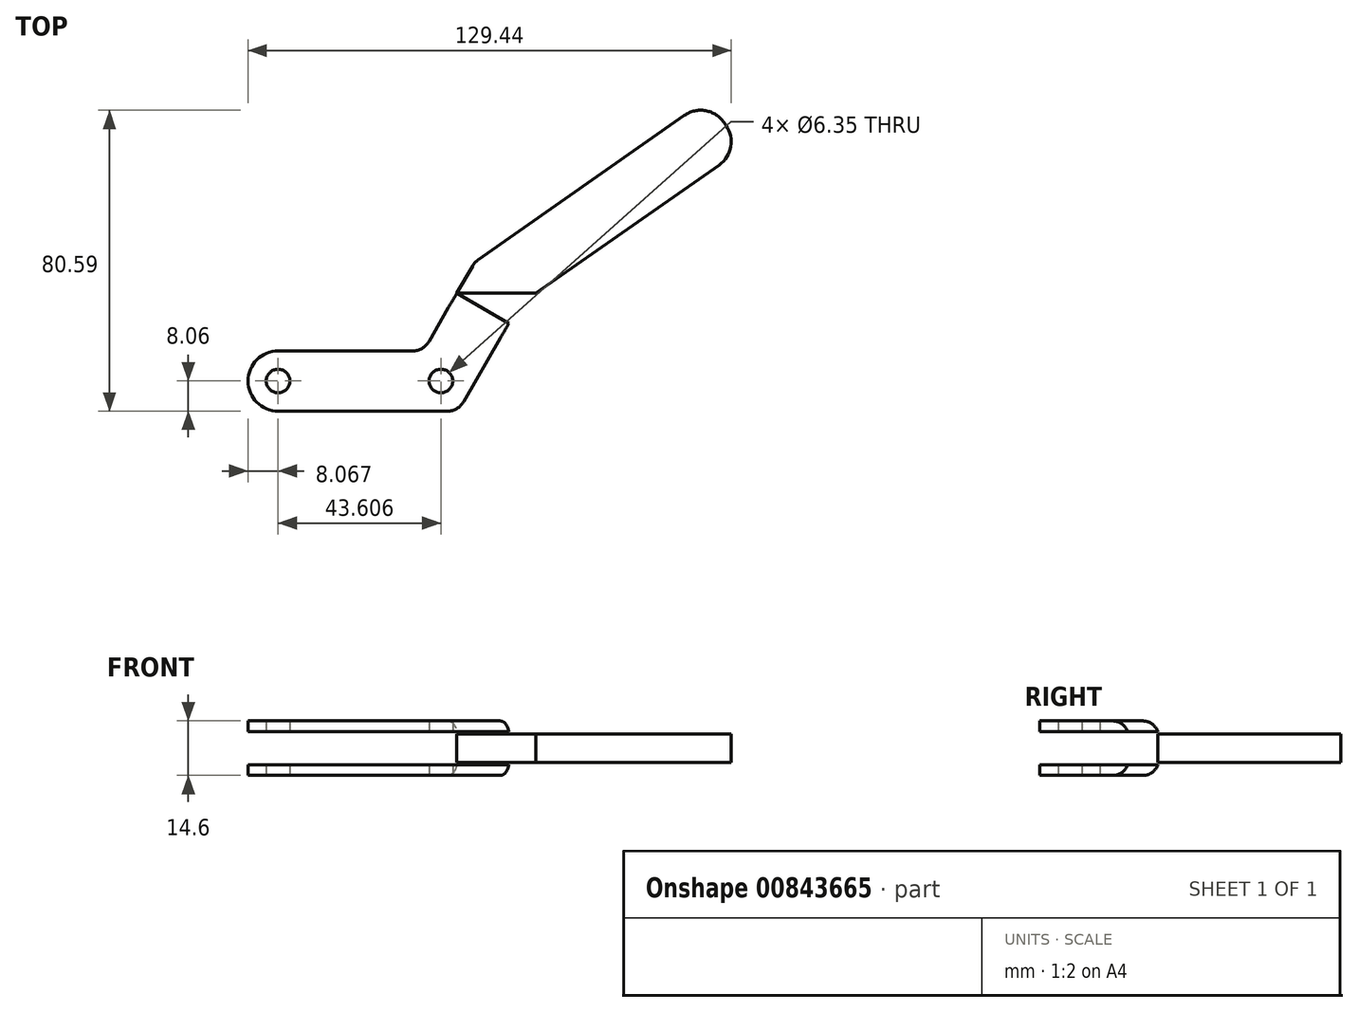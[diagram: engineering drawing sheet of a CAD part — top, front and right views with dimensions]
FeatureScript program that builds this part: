
annotation { "Feature Type Name" : "Feature", "Feature Type Description" : "" }
export const myFeature = defineFeature(function(context is Context, id is Id, definition is map)
    precondition{}
    {
        {
            var Q0;
            Q0=qCreatedBy(makeId("Top.planeOp"),FACE);
            var sketch = newSketch(context, id + "F0", { "sketchPlane" : qUnion([Q0])});
            skLineSegment(sketch, "E0.bottom", {"start": v(21.8, 8.06) * mm, "end": v(-21.8, 8.06) * mm});
            skLineSegment(sketch, "E0.top", {"start": v(21.8, -8.06) * mm, "end": v(-21.8, -8.06) * mm, "construction": true});
            skPoint(sketch, "E0.middle", {"position": v(0, 0) * mm});
            skArc(sketch, "E1", {"start": v(-21.8, 8.06) * mm, "mid": v(-29.87, 0) * mm, "end": v(-21.8, -8.06) * mm});
            skLineSegment(sketch, "E2", {"start": v(14.35, 3.22) * mm, "end": v(30.86, 31.82) * mm, "construction": true});
            skLineSegment(sketch, "E3", {"start": v(42.97, 20.53) * mm, "end": v(26.46, -8.06) * mm});
            skLineSegment(sketch, "E4", {"start": v(26.46, -8.06) * mm, "end": v(14.35, 3.22) * mm, "construction": true});
            skLineSegment(sketch, "E5", {"start": v(30.86, 31.82) * mm, "end": v(42.97, 20.53) * mm, "construction": true});
            skLineSegment(sketch, "E6", {"start": v(30.86, 31.82) * mm, "end": v(93.28, 75.53) * mm});
            skLineSegment(sketch, "E7", {"start": v(102.57, 62.26) * mm, "end": v(42.97, 20.53) * mm});
            skCircle(sketch, "E8", {"center": v(-21.8, 0) * mm, "radius": 3.18 * mm});
            skCircle(sketch, "E9", {"center": v(21.8, 0) * mm, "radius": 3.18 * mm});
            skLineSegment(sketch, "E10", {"start": v(26.46, -8.06) * mm, "end": v(21.8, -8.06) * mm});
            skLineSegment(sketch, "E11", {"start": v(21.8, -8.06) * mm, "end": v(-21.8, -8.06) * mm});
            skLineSegment(sketch, "E12", {"start": v(-21.8, 8.06) * mm, "end": v(17.15, 8.06) * mm});
            skLineSegment(sketch, "E13", {"start": v(17.15, 8.06) * mm, "end": v(30.86, 31.82) * mm});
            skLineSegment(sketch, "E14", {"start": v(93.28, 75.53) * mm, "end": v(102.57, 62.26) * mm});
            skArc(sketch, "E15", {"start": v(28.71, -4.16) * mm, "mid": v(28.82, 3.97) * mm, "end": v(21.8, 8.06) * mm});
            skSolve(sketch);
        }
        {
            var Q0;
            {var subQ0=sQuery(id+"F0.wireOp",EDGE,"E15");var subQ1=sQuery(id+"F0.wireOp",EDGE,"E3");var subQ2=makeQuery(id+"F0.imprint","INTERSECT",VERTEX,{"disambiguationData":[OD(0.0)],"derivedFrom":[subQ1,subQ0]});var subQ8=sQuery(id+"F0.wireOp",EDGE,"E1");var subQ12=makeQuery(id+"F0.imprint","IMPRINT",EDGE,{"disambiguationData":[TD([[subQ2,1.0]])],"derivedFrom":subQ1});Q0=qUnion([makeQuery(id+"F0.imprint","IMPRINT",FACE,{"disambiguationData":[TD([[makeQuery(id+"F0.imprint","IMPRINT",EDGE,{"derivedFrom":sQuery(id+"F0.wireOp",EDGE,"E6")}),-1.0]])]}),makeQuery(id+"F0.imprint","IMPRINT",FACE,{"disambiguationData":[TD([[subQ12,1.0]])]}),makeQuery(id+"F0.imprint","IMPRINT",FACE,{"disambiguationData":[TD([[makeQuery(id+"F0.imprint","IMPRINT",EDGE,{"derivedFrom":subQ8}),1.0]])]})]);}
            extrude(context, id + "F1", {"entities" : qUnion([Q0]), "depth" : 7.62 * mm / 2, "offsetDistance" : 25.4 * mm, "hasSecondDirection" : true, "secondDirectionOppositeDirection" : true, "secondDirectionDepth" : 7.62 * mm / 2});
        }
        {
            var Q0;
            Q0=makeQuery(id+"F1.opExtrude","CAP_FACE",FACE,{"disambiguationData":[OSD([sQuery(id+"F0.wireOp",EDGE,"E0.bottom"),sQuery(id+"F0.wireOp",EDGE,"E1"),sQuery(id+"F0.wireOp",EDGE,"E3"),sQuery(id+"F0.wireOp",EDGE,"E6"),sQuery(id+"F0.wireOp",EDGE,"E7"),sQuery(id+"F0.wireOp",EDGE,"E8"),sQuery(id+"F0.wireOp",EDGE,"E9"),sQuery(id+"F0.wireOp",EDGE,"E10"),sQuery(id+"F0.wireOp",EDGE,"E11"),sQuery(id+"F0.wireOp",EDGE,"E13"),sQuery(id+"F0.wireOp",EDGE,"E14"),sQuery(id+"F0.wireOp",EDGE,"E15")])],"isStart":false});
            var sketch = newSketch(context, id + "F2", { "sketchPlane" : qUnion([Q0])});
            skPoint(sketch, "E16.0", {"position": v(-2.33, 8.06) * mm});
            skArc(sketch, "E17.0", {"start": v(-21.8, 8.06) * mm, "mid": v(-29.87, 0) * mm, "end": v(-21.8, -8.06) * mm});
            skLineSegment(sketch, "E18.0", {"start": v(26.46, -8.06) * mm, "end": v(-21.8, -8.06) * mm});
            skLineSegment(sketch, "E19.0", {"start": v(-21.8, 8.06) * mm, "end": v(17.15, 8.06) * mm});
            skLineSegment(sketch, "E20.0", {"start": v(28.71, -4.16) * mm, "end": v(26.46, -8.06) * mm});
            skLineSegment(sketch, "E21.0", {"start": v(21.8, 8.06) * mm, "end": v(-21.8, 8.06) * mm});
            skPoint(sketch, "E22.orphan", {"position": v(42.97, 20.53) * mm});
            skCircle(sketch, "E23.0", {"center": v(-21.8, 0) * mm, "radius": 3.18 * mm});
            skCircle(sketch, "E24.0", {"center": v(21.8, 0) * mm, "radius": 3.18 * mm});
            skArc(sketch, "E25.0", {"start": v(28.71, -4.16) * mm, "mid": v(28.82, 3.97) * mm, "end": v(21.8, 8.06) * mm});
            skSolve(sketch);
        }
        {
            var Q0;
            {var subQ1=sQuery(id+"F2.wireOp",EDGE,"E17.0");Q0=makeQuery(id+"F2.imprint","IMPRINT",FACE,{"disambiguationData":[TD([[makeQuery(id+"F2.imprint","IMPRINT",EDGE,{"derivedFrom":subQ1}),1.0]])]});}
            extrude(context, id + "F3", {"entities" : qUnion([Q0]), "operationType" : NewBodyOperationType.ADD, "depth" : 7 * mm / 2, "offsetDistance" : 25.4 * mm, "hasSecondDirection" : true, "secondDirectionOppositeDirection" : true, "secondDirectionDepth" : 22.22 * mm / 2});
        }
        {
            var Q0;
            Q0=makeQuery(id+"F3.boolean.opBoolean","MERGE",FACE,{"derivedFrom":[makeQuery(id+"F1.opExtrude","SWEPT_FACE",FACE,{"disambiguationData":[OSD([sQuery(id+"F0.wireOp",EDGE,"E10"),sQuery(id+"F0.wireOp",EDGE,"E11")])]}),makeQuery(id+"F3.opExtrude","SWEPT_FACE",FACE,{"disambiguationData":[OSD([sQuery(id+"F2.wireOp",EDGE,"E18.0")])]})]});
            var sketch = newSketch(context, id + "F4", { "sketchPlane" : qUnion([Q0])});
            skLineSegment(sketch, "E26.bottom", {"start": v(57.45, 4.45) * mm, "end": v(-57.45, 4.45) * mm});
            skLineSegment(sketch, "E26.top", {"start": v(57.45, -4.45) * mm, "end": v(-57.45, -4.45) * mm});
            skLineSegment(sketch, "E26.left", {"start": v(57.45, 4.45) * mm, "end": v(57.45, -4.45) * mm});
            skLineSegment(sketch, "E26.right", {"start": v(-57.45, 4.45) * mm, "end": v(-57.45, -4.45) * mm});
            skPoint(sketch, "E26.middle", {"position": v(0, 0) * mm});
            skSolve(sketch);
        }
        {
            var Q0;
            Q0=makeQuery(id+"F3.boolean.opBoolean","MERGE",EDGE,{"derivedFrom":[makeQuery(id+"F1.opExtrude","SWEPT_EDGE",EDGE,{"disambiguationData":[OSD([sQuery(id+"F0.wireOp",EDGE,"E3"),sQuery(id+"F0.wireOp",EDGE,"E10")])]}),makeQuery(id+"F3.opExtrude","SWEPT_EDGE",EDGE,{"disambiguationData":[OSD([sQuery(id+"F2.wireOp",EDGE,"E18.0"),sQuery(id+"F2.wireOp",EDGE,"E20.0")])]})]});
            var Q1;
            Q1=makeQuery(id+"F1.opExtrude","SWEPT_EDGE",EDGE,{"disambiguationData":[OSD([sQuery(id+"F0.wireOp",EDGE,"E0.bottom"),sQuery(id+"F0.wireOp",EDGE,"E13")])]});
            fillet(context, id + "F5", {"entities" : qUnion([Q0, Q1]), "radius" : 5.08 * mm, "tangentPropagation" : true, "allowEdgeOverflow" : false});
        }
        {
            var Q0;
            Q0=makeQuery(id+"F1.opExtrude","SWEPT_EDGE",EDGE,{"disambiguationData":[OSD([sQuery(id+"F0.wireOp",EDGE,"E6"),sQuery(id+"F0.wireOp",EDGE,"E14")])]});
            var Q1;
            Q1=makeQuery(id+"F1.opExtrude","SWEPT_EDGE",EDGE,{"disambiguationData":[OSD([sQuery(id+"F0.wireOp",EDGE,"E7"),sQuery(id+"F0.wireOp",EDGE,"E14")])]});
            fillet(context, id + "F6", {"entities" : qUnion([Q0, Q1]), "radius" : 7.62 * mm, "tangentPropagation" : true, "allowEdgeOverflow" : false});
        }
        {
            var Q0;
            Q0=qCreatedBy(makeId("Top.planeOp"),FACE);
            var sketch = newSketch(context, id + "F7", { "sketchPlane" : qUnion([Q0])});
            skLineSegment(sketch, "E27.0", {"start": v(18.61, 10.6) * mm, "end": v(26.09, 23.56) * mm});
            skArc(sketch, "E28.0", {"start": v(18.61, 10.6) * mm, "mid": v(16.75, 8.75) * mm, "end": v(14.21, 8.06) * mm});
            skLineSegment(sketch, "E29.0", {"start": v(21.8, 8.06) * mm, "end": v(14.21, 8.06) * mm});
            skArc(sketch, "E30.0", {"start": v(28.71, -4.16) * mm, "mid": v(28.82, 3.97) * mm, "end": v(21.8, 8.06) * mm});
            skLineSegment(sketch, "E31", {"start": v(40.06, 15.5) * mm, "end": v(26.09, 23.56) * mm});
            skPoint(sketch, "E32.orphan", {"position": v(-21.8, 8.06) * mm});
            skLineSegment(sketch, "E33.0", {"start": v(40.06, 15.5) * mm, "end": v(28.86, -3.9) * mm});
            skPoint(sketch, "E34.orphan", {"position": v(42.97, 20.53) * mm});
            skPoint(sketch, "E35.orphan", {"position": v(30.86, 31.82) * mm});
            skSolve(sketch);
        }
        {
            var Q0;
            Q0 = qSketchRegion(id + "F7", true);
            var Q1;
            Q1=makeQuery(id+"F3.opExtrude","CAP_VERTEX",VERTEX,{"disambiguationData":[OSD([sQuery(id+"F2.wireOp",EDGE,"E21.0"),sQuery(id+"F2.wireOp",EDGE,"E25.0")])],"isStart":false});
            var Q2;
            Q2=makeQuery(id+"F3.opExtrude","CAP_VERTEX",VERTEX,{"disambiguationData":[OSD([sQuery(id+"F2.wireOp",EDGE,"E21.0"),sQuery(id+"F2.wireOp",EDGE,"E25.0")])],"isStart":true});
            extrude(context, id + "F8", {"entities" : qUnion([Q0]), "operationType" : NewBodyOperationType.ADD, "endBound" : BoundingType.UP_TO_VERTEX, "depth" : 25.4 * mm, "endBoundEntityVertex" : qUnion([Q1]), "offsetDistance" : 25.4 * mm, "hasSecondDirection" : true, "secondDirectionBound" : BoundingType.UP_TO_VERTEX, "secondDirectionOppositeDirection" : true, "secondDirectionDepth" : 25.4 * mm, "secondDirectionBoundEntityVertex" : qUnion([Q2])});
        }
        {
            var Q0;
            {var subQ0=sQuery(id+"F4.wireOp",EDGE,"E26.right");Q0=makeQuery(id+"F4.imprint","IMPRINT",FACE,{"disambiguationData":[TD([[makeQuery(id+"F4.imprint","IMPRINT",EDGE,{"derivedFrom":subQ0}),1.0]])]});}
            var Q1;
            {var subQ0=sQuery(id+"F4.wireOp",EDGE,"E26.bottom");var subQ1=sQuery(id+"F2.wireOp",EDGE,"E18.0");var subQ2=makeQuery(id+"F3.boolean.opBoolean","MERGE",EDGE,{"derivedFrom":[makeQuery(id+"F1.opExtrude","SWEPT_EDGE",EDGE,{"disambiguationData":[OSD([sQuery(id+"F0.wireOp",EDGE,"E3"),sQuery(id+"F0.wireOp",EDGE,"E10")])]}),makeQuery(id+"F3.opExtrude","SWEPT_EDGE",EDGE,{"disambiguationData":[OSD([subQ1,sQuery(id+"F2.wireOp",EDGE,"E20.0")])]})]});var subQ3=makeQuery(id+"F4.imprint","INTERSECT",VERTEX,{"derivedFrom":[subQ2,subQ0]});Q1=makeQuery(id+"F4.imprint","IMPRINT",FACE,{"disambiguationData":[TD([[makeQuery(id+"F4.imprint","IMPRINT",EDGE,{"disambiguationData":[TD([[subQ3,-1.0]])],"derivedFrom":subQ0}),1.0]])]});}
            var Q2;
            {var subQ0=sQuery(id+"F4.wireOp",EDGE,"E26.left");Q2=makeQuery(id+"F4.imprint","IMPRINT",FACE,{"disambiguationData":[TD([[makeQuery(id+"F4.imprint","IMPRINT",EDGE,{"derivedFrom":subQ0}),-1.0]])]});}
            var Q3;
            Q3=makeQuery(id+"F8.boolean.opBoolean","INTERSECT",VERTEX,{"disambiguationData":[OD(0.0)],"derivedFrom":[makeQuery(id+"F1.opExtrude","CAP_FACE",FACE,{"disambiguationData":[OSD([sQuery(id+"F0.wireOp",EDGE,"E0.bottom"),sQuery(id+"F0.wireOp",EDGE,"E1"),sQuery(id+"F0.wireOp",EDGE,"E3"),sQuery(id+"F0.wireOp",EDGE,"E6"),sQuery(id+"F0.wireOp",EDGE,"E7"),sQuery(id+"F0.wireOp",EDGE,"E8"),sQuery(id+"F0.wireOp",EDGE,"E9"),sQuery(id+"F0.wireOp",EDGE,"E10"),sQuery(id+"F0.wireOp",EDGE,"E11"),sQuery(id+"F0.wireOp",EDGE,"E13"),sQuery(id+"F0.wireOp",EDGE,"E14"),sQuery(id+"F0.wireOp",EDGE,"E15")])],"isStart":false}),makeQuery(id+"F8.opExtrude","SWEPT_FACE",FACE,{"disambiguationData":[OSD([sQuery(id+"F7.wireOp",EDGE,"E31")])]})]});
            extrude(context, id + "F9", {"entities" : qUnion([Q0, Q1, Q2]), "operationType" : NewBodyOperationType.REMOVE, "endBound" : BoundingType.UP_TO_VERTEX, "oppositeDirection" : true, "depth" : 25.4 * mm, "endBoundEntityVertex" : qUnion([Q3]), "offsetDistance" : 25.4 * mm});
        }
        {
            var Q0;
            Q0=makeQuery(id+"F8.opExtrude","CAP_EDGE",EDGE,{"disambiguationData":[OSD([sQuery(id+"F7.wireOp",EDGE,"E31")])],"isStart":true});
            var Q1;
            Q1=makeQuery(id+"F8.opExtrude","CAP_EDGE",EDGE,{"disambiguationData":[OSD([sQuery(id+"F7.wireOp",EDGE,"E31")])],"isStart":false});
            var Q2;
            Q2=makeQuery(id+"F1.opExtrude","SWEPT_EDGE",EDGE,{"disambiguationData":[OSD([sQuery(id+"F0.wireOp",EDGE,"E6"),sQuery(id+"F0.wireOp",EDGE,"E13")])]});
            var Q3;
            Q3=makeQuery(id+"F1.opExtrude","SWEPT_EDGE",EDGE,{"disambiguationData":[OSD([sQuery(id+"F0.wireOp",EDGE,"E3"),sQuery(id+"F0.wireOp",EDGE,"E7")])]});
            fillet(context, id + "F10", {"entities" : qUnion([Q0, Q1, Q2, Q3]), "radius" : 5.08 * mm, "tangentPropagation" : true, "allowEdgeOverflow" : false});
        }
    });
